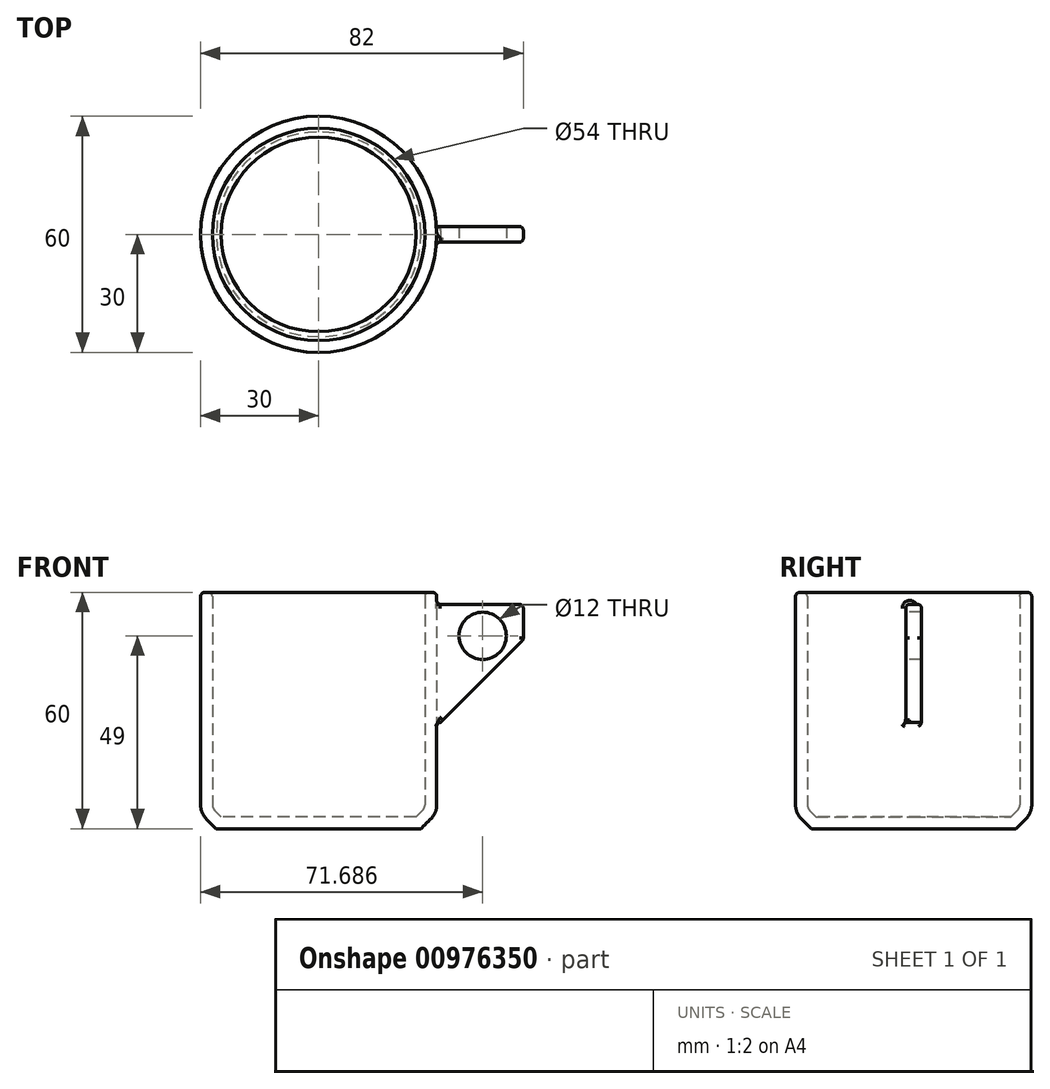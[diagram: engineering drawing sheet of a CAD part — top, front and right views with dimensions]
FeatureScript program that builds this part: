
annotation { "Feature Type Name" : "Feature", "Feature Type Description" : "" }
export const myFeature = defineFeature(function(context is Context, id is Id, definition is map)
    precondition{}
    {
        {
            var Q0;
            Q0=qCreatedBy(makeId("Top.planeOp"),FACE);
            var sketch = newSketch(context, id + "F0", { "sketchPlane" : qUnion([Q0])});
            skCircle(sketch, "E0", {"center": v(0, 0) * mm, "radius": 30 * mm});
            skSolve(sketch);
        }
        {
            var Q0;
            Q0=makeQuery(id+"F0.imprint","IMPRINT",FACE,{"disambiguationData":[TD([[makeQuery(id+"F0.imprint","IMPRINT",EDGE,{"derivedFrom":sQuery(id+"F0.wireOp",EDGE,"E0")}),1.0]])]});
            extrude(context, id + "F1", {"entities" : qUnion([Q0]), "depth" : 60 * mm, "offsetDistance" : 25 * mm});
        }
        {
            var Q0;
            Q0=makeQuery(id+"F1.opExtrude","CAP_EDGE",EDGE,{"disambiguationData":[OSD([sQuery(id+"F0.wireOp",EDGE,"E0")])],"isStart":true});
            chamfer(context, id + "F2", {"entities" : qUnion([Q0]), "width" : 4 * mm, "tangentPropagation" : true});
        }
        {
            var Q0;
            {var subQ0=sQuery(id+"F0.wireOp",EDGE,"E0");Q0=makeQuery(id+"F2.opChamfer","BLEND_EDGE",EDGE,{"blendedFrom":[makeQuery(id+"F1.opExtrude","CAP_EDGE",EDGE,{"disambiguationData":[OSD([subQ0])],"isStart":true}),makeQuery(id+"F1.opExtrude","SWEPT_FACE",FACE,{"disambiguationData":[OSD([subQ0])]})],"blendedInto":[makeQuery(id+"F1.opExtrude","SWEPT_FACE",FACE,{"disambiguationData":[OSD([subQ0])]})]});}
            fillet(context, id + "F3", {"entities" : qUnion([Q0]), "radius" : 5 * mm, "tangentPropagation" : true, "allowEdgeOverflow" : false});
        }
        {
            var Q0;
            Q0=makeQuery(id+"F1.opExtrude","CAP_FACE",FACE,{"disambiguationData":[OSD([sQuery(id+"F0.wireOp",EDGE,"E0")])],"isStart":false});
            shell(context, id + "F4", {"entities" : qUnion([Q0]), "thickness" : 3 * mm});
        }
        {
            var Q0;
            Q0=qCreatedBy(makeId("Front.planeOp"),FACE);
            var sketch = newSketch(context, id + "F5", { "sketchPlane" : qUnion([Q0])});
            skLineSegment(sketch, "E1.bottom", {"start": v(27, 57) * mm, "end": v(52, 57) * mm});
            skLineSegment(sketch, "E1.top", {"start": v(27, 27) * mm, "end": v(52, 27) * mm});
            skLineSegment(sketch, "E1.left", {"start": v(27, 57) * mm, "end": v(27, 27) * mm});
            skLineSegment(sketch, "E1.right", {"start": v(52, 57) * mm, "end": v(52, 27) * mm});
            skSolve(sketch);
        }
        {
            var Q0;
            Q0 = qSketchRegion(id + "F5", true);
            extrude(context, id + "F6", {"entities" : qUnion([Q0]), "operationType" : NewBodyOperationType.ADD, "endBound" : BoundingType.SYMMETRIC, "depth" : 4 * mm, "offsetDistance" : 25 * mm});
        }
        {
            var Q0;
            Q0=makeQuery(id+"F6.opExtrude","SWEPT_EDGE",EDGE,{"disambiguationData":[OSD([sQuery(id+"F5.wireOp",EDGE,"E1.top"),sQuery(id+"F5.wireOp",EDGE,"E1.right")])]});
            chamfer(context, id + "F7", {"entities" : qUnion([Q0]), "width" : 21 * mm, "tangentPropagation" : true});
        }
        {
            var Q0;
            Q0=makeQuery(id+"F6.opExtrude","CAP_FACE",FACE,{"disambiguationData":[OSD([sQuery(id+"F5.wireOp",EDGE,"E1.bottom"),sQuery(id+"F5.wireOp",EDGE,"E1.top"),sQuery(id+"F5.wireOp",EDGE,"E1.left"),sQuery(id+"F5.wireOp",EDGE,"E1.right")])],"isStart":false});
            var sketch = newSketch(context, id + "F8", { "sketchPlane" : qUnion([Q0])});
            skCircle(sketch, "E2", {"center": v(41.69, 49) * mm, "radius": 6 * mm});
            skSolve(sketch);
        }
        {
            var Q0;
            Q0 = qSketchRegion(id + "F8", true);
            extrude(context, id + "F9", {"entities" : qUnion([Q0]), "operationType" : NewBodyOperationType.REMOVE, "endBound" : BoundingType.THROUGH_ALL, "oppositeDirection" : true, "depth" : 25 * mm, "offsetDistance" : 25 * mm});
        }
        {
            var Q0;
            Q0=makeQuery(id+"F6.boolean.opBoolean","INTERSECT",EDGE,{"derivedFrom":[makeQuery(id+"F1.opExtrude","SWEPT_FACE",FACE,{"disambiguationData":[OSD([sQuery(id+"F0.wireOp",EDGE,"E0")])]}),makeQuery(id+"F6.opExtrude","CAP_FACE",FACE,{"disambiguationData":[OSD([sQuery(id+"F5.wireOp",EDGE,"E1.bottom"),sQuery(id+"F5.wireOp",EDGE,"E1.top"),sQuery(id+"F5.wireOp",EDGE,"E1.left"),sQuery(id+"F5.wireOp",EDGE,"E1.right")])],"isStart":false})]});
            var Q1;
            Q1=makeQuery(id+"F6.boolean.opBoolean","INTERSECT",EDGE,{"derivedFrom":[makeQuery(id+"F1.opExtrude","SWEPT_FACE",FACE,{"disambiguationData":[OSD([sQuery(id+"F0.wireOp",EDGE,"E0")])]}),makeQuery(id+"F6.opExtrude","SWEPT_FACE",FACE,{"disambiguationData":[OSD([sQuery(id+"F5.wireOp",EDGE,"E1.top")])]})]});
            var Q2;
            Q2=makeQuery(id+"F6.opExtrude","CAP_EDGE",EDGE,{"disambiguationData":[OSD([sQuery(id+"F5.wireOp",EDGE,"E1.bottom")])],"isStart":false});
            var Q3;
            Q3=makeQuery(id+"F6.opExtrude","CAP_EDGE",EDGE,{"disambiguationData":[OSD([sQuery(id+"F5.wireOp",EDGE,"E1.bottom")])],"isStart":true});
            var Q4;
            Q4=makeQuery(id+"F6.opExtrude","SWEPT_EDGE",EDGE,{"disambiguationData":[OSD([sQuery(id+"F5.wireOp",EDGE,"E1.bottom"),sQuery(id+"F5.wireOp",EDGE,"E1.right")])]});
            var Q5;
            Q5=makeQuery(id+"F6.opExtrude","CAP_EDGE",EDGE,{"disambiguationData":[OSD([sQuery(id+"F5.wireOp",EDGE,"E1.right")])],"isStart":false});
            var Q6;
            Q6=makeQuery(id+"F6.opExtrude","CAP_EDGE",EDGE,{"disambiguationData":[OSD([sQuery(id+"F5.wireOp",EDGE,"E1.right")])],"isStart":true});
            fillet(context, id + "F10", {"entities" : qUnion([Q0, Q1, Q2, Q3, Q4, Q5, Q6]), "radius" : 1 * mm, "tangentPropagation" : true, "allowEdgeOverflow" : false});
        }
        {
            var Q0;
            {var subQ0=sQuery(id+"F5.wireOp",EDGE,"E1.right");var subQ1=sQuery(id+"F5.wireOp",EDGE,"E1.top");Q0=makeQuery(id+"F7.opChamfer","BLEND_EDGE",EDGE,{"blendedFrom":[makeQuery(id+"F6.opExtrude","SWEPT_EDGE",EDGE,{"disambiguationData":[OSD([subQ1,subQ0])]}),makeQuery(id+"F6.opExtrude","CAP_FACE",FACE,{"disambiguationData":[OSD([sQuery(id+"F5.wireOp",EDGE,"E1.bottom"),subQ1,sQuery(id+"F5.wireOp",EDGE,"E1.left"),subQ0])],"isStart":false})],"blendedInto":[makeQuery(id+"F6.opExtrude","CAP_FACE",FACE,{"disambiguationData":[OSD([sQuery(id+"F5.wireOp",EDGE,"E1.bottom"),subQ1,sQuery(id+"F5.wireOp",EDGE,"E1.left"),subQ0])],"isStart":false})]});}
            fillet(context, id + "F11", {"entities" : qUnion([Q0]), "radius" : 1 * mm, "tangentPropagation" : true, "allowEdgeOverflow" : false});
        }
        {
            var Q0;
            {var subQ0=sQuery(id+"F0.wireOp",EDGE,"E0");Q0=makeQuery(id+"F4.opShell","OFFSET_EDGE",EDGE,{"disambiguationData":[OSD([subQ0]),TDD([makeQuery(id+"F1.opExtrude","CAP_EDGE",EDGE,{"disambiguationData":[OSD([subQ0])],"isStart":false})])]});}
            var Q1;
            Q1=makeQuery(id+"F1.opExtrude","CAP_EDGE",EDGE,{"disambiguationData":[OSD([sQuery(id+"F0.wireOp",EDGE,"E0")])],"isStart":false});
            fillet(context, id + "F12", {"entities" : qUnion([Q0, Q1]), "radius" : 1 * mm, "tangentPropagation" : true, "allowEdgeOverflow" : false});
        }
    });
